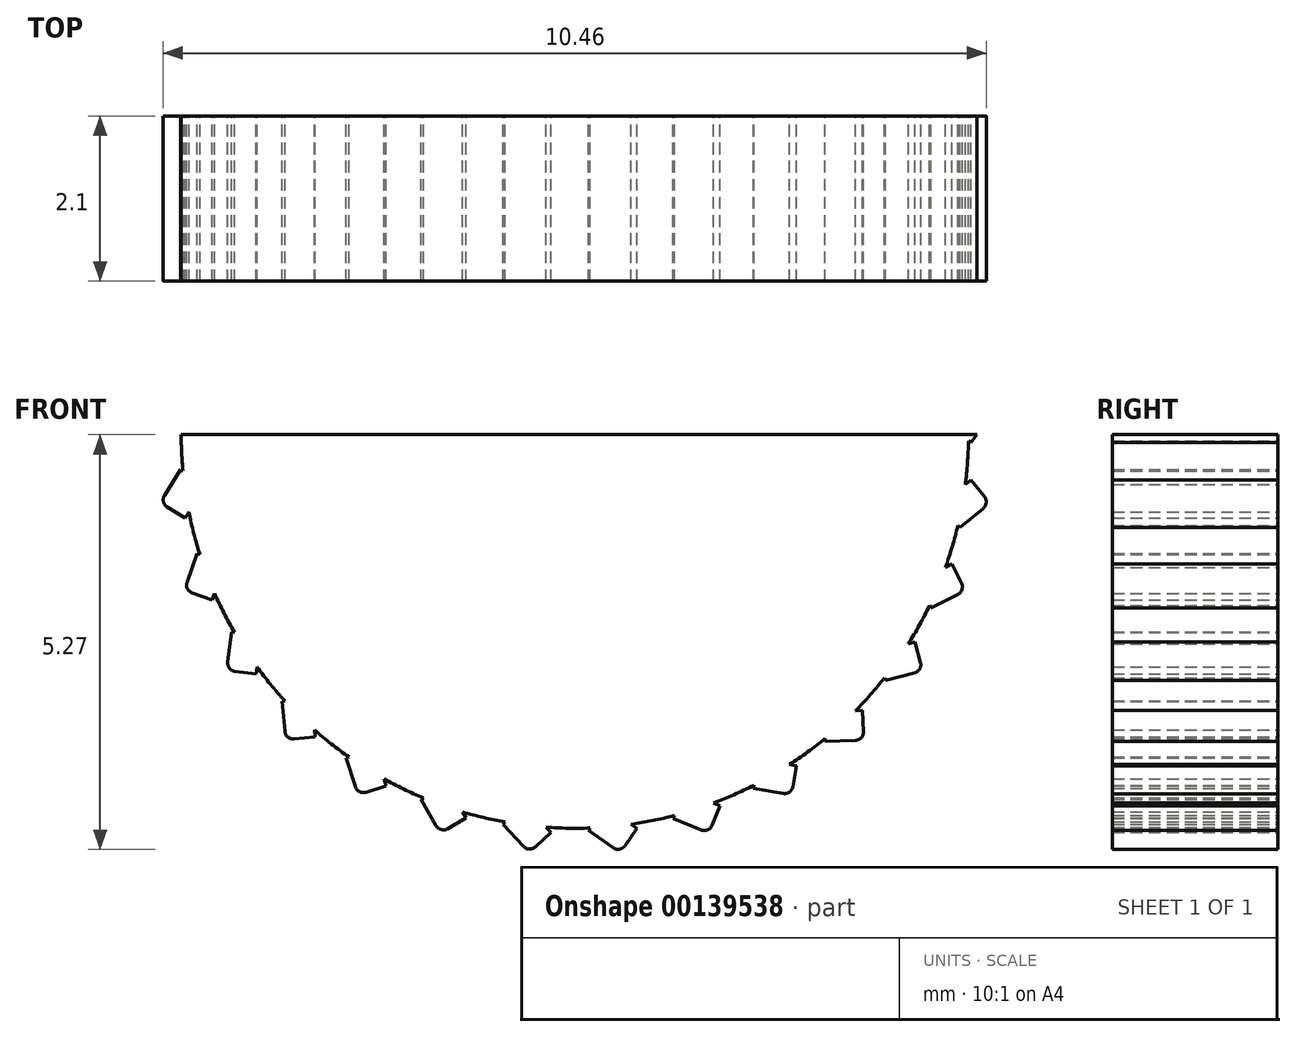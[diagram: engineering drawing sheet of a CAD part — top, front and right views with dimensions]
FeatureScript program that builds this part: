
annotation { "Feature Type Name" : "Feature", "Feature Type Description" : "" }
export const myFeature = defineFeature(function(context is Context, id is Id, definition is map)
    precondition{}
    {
        {
            var Q0;
            Q0=qCreatedBy(makeId("Front.planeOp"),FACE);
            var sketch = newSketch(context, id + "F0", { "sketchPlane" : qUnion([Q0])});
            skCircle(sketch, "E0", {"center": v(0, 0) * mm, "radius": 5 * mm});
            skPoint(sketch, "E1.0.29.0", {"position": v(-5.33, 0.3) * mm});
            skLineSegment(sketch, "E1.1.29.0", {"start": v(-4.72, 0.38) * mm, "end": v(-4.99, 0.64) * mm});
            skLineSegment(sketch, "E1.4.29.0", {"start": v(-5.26, 0.37) * mm, "end": v(-4.99, 0.64) * mm});
            skLineSegment(sketch, "E1.7.29.0", {"start": v(-5.06, 0.03) * mm, "end": v(-4.72, 0.38) * mm});
            skLineSegment(sketch, "E1.10.29.0", {"start": v(-5.06, 0.03) * mm, "end": v(-5.26, 0.22) * mm});
            skArc(sketch, "E1.13.29.0", {"start": v(-5.26, 0.37) * mm, "mid": v(-5.29, 0.3) * mm, "end": v(-5.26, 0.22) * mm});
            skPoint(sketch, "E2.1.0", {"position": v(-5.14, 1.43) * mm});
            skLineSegment(sketch, "E2.1.1", {"start": v(-4.94, 1.12) * mm, "end": v(-4.53, 1.39) * mm});
            skLineSegment(sketch, "E2.1.2", {"start": v(-4.94, 1.12) * mm, "end": v(-5.09, 1.34) * mm});
            skLineSegment(sketch, "E2.1.3", {"start": v(-4.53, 1.39) * mm, "end": v(-4.73, 1.7) * mm});
            skLineSegment(sketch, "E2.1.4", {"start": v(-5.06, 1.49) * mm, "end": v(-4.73, 1.7) * mm});
            skArc(sketch, "E2.1.5", {"start": v(-5.06, 1.49) * mm, "mid": v(-5.1, 1.42) * mm, "end": v(-5.09, 1.34) * mm});
            skPoint(sketch, "E2.2.0", {"position": v(-4.72, 2.5) * mm});
            skLineSegment(sketch, "E2.2.1", {"start": v(-4.58, 2.15) * mm, "end": v(-4.12, 2.33) * mm});
            skLineSegment(sketch, "E2.2.2", {"start": v(-4.58, 2.15) * mm, "end": v(-4.68, 2.4) * mm});
            skLineSegment(sketch, "E2.2.3", {"start": v(-4.12, 2.33) * mm, "end": v(-4.26, 2.68) * mm});
            skLineSegment(sketch, "E2.2.4", {"start": v(-4.62, 2.54) * mm, "end": v(-4.26, 2.68) * mm});
            skArc(sketch, "E2.2.5", {"start": v(-4.62, 2.54) * mm, "mid": v(-4.68, 2.49) * mm, "end": v(-4.68, 2.4) * mm});
            skPoint(sketch, "E2.3.0", {"position": v(-4.07, 3.46) * mm});
            skLineSegment(sketch, "E2.3.1", {"start": v(-4.01, 3.09) * mm, "end": v(-3.53, 3.16) * mm});
            skLineSegment(sketch, "E2.3.2", {"start": v(-4.01, 3.09) * mm, "end": v(-4.05, 3.35) * mm});
            skLineSegment(sketch, "E2.3.3", {"start": v(-3.53, 3.16) * mm, "end": v(-3.58, 3.53) * mm});
            skLineSegment(sketch, "E2.3.4", {"start": v(-3.96, 3.47) * mm, "end": v(-3.58, 3.53) * mm});
            skArc(sketch, "E2.3.5", {"start": v(-3.96, 3.47) * mm, "mid": v(-4.03, 3.43) * mm, "end": v(-4.05, 3.35) * mm});
            skPoint(sketch, "E2.4.0", {"position": v(-3.23, 4.25) * mm});
            skLineSegment(sketch, "E2.4.1", {"start": v(-3.25, 3.88) * mm, "end": v(-2.76, 3.84) * mm});
            skLineSegment(sketch, "E2.4.2", {"start": v(-3.25, 3.88) * mm, "end": v(-3.24, 4.15) * mm});
            skLineSegment(sketch, "E2.4.3", {"start": v(-2.76, 3.84) * mm, "end": v(-2.74, 4.22) * mm});
            skLineSegment(sketch, "E2.4.4", {"start": v(-3.12, 4.25) * mm, "end": v(-2.74, 4.22) * mm});
            skArc(sketch, "E2.4.5", {"start": v(-3.12, 4.25) * mm, "mid": v(-3.2, 4.22) * mm, "end": v(-3.24, 4.15) * mm});
            skPoint(sketch, "E2.5.0", {"position": v(-2.24, 4.85) * mm});
            skLineSegment(sketch, "E2.5.1", {"start": v(-2.34, 4.49) * mm, "end": v(-1.87, 4.35) * mm});
            skLineSegment(sketch, "E2.5.2", {"start": v(-2.34, 4.49) * mm, "end": v(-2.27, 4.75) * mm});
            skLineSegment(sketch, "E2.5.3", {"start": v(-1.87, 4.35) * mm, "end": v(-1.77, 4.7) * mm});
            skLineSegment(sketch, "E2.5.4", {"start": v(-2.14, 4.82) * mm, "end": v(-1.77, 4.7) * mm});
            skArc(sketch, "E2.5.5", {"start": v(-2.14, 4.82) * mm, "mid": v(-2.22, 4.8) * mm, "end": v(-2.27, 4.75) * mm});
            skPoint(sketch, "E2.6.0", {"position": v(-1.15, 5.22) * mm});
            skLineSegment(sketch, "E2.6.1", {"start": v(-1.33, 4.89) * mm, "end": v(-0.9, 4.65) * mm});
            skLineSegment(sketch, "E2.6.2", {"start": v(-1.33, 4.89) * mm, "end": v(-1.2, 5.12) * mm});
            skLineSegment(sketch, "E2.6.3", {"start": v(-0.9, 4.65) * mm, "end": v(-0.71, 4.98) * mm});
            skLineSegment(sketch, "E2.6.4", {"start": v(-1.05, 5.16) * mm, "end": v(-0.71, 4.98) * mm});
            skArc(sketch, "E2.6.5", {"start": v(-1.05, 5.16) * mm, "mid": v(-1.13, 5.17) * mm, "end": v(-1.2, 5.12) * mm});
            skPoint(sketch, "E2.7.0", {"position": v(0, 5.34) * mm});
            skLineSegment(sketch, "E2.7.1", {"start": v(-0.24, 5.06) * mm, "end": v(0.13, 4.73) * mm});
            skLineSegment(sketch, "E2.7.2", {"start": v(-0.24, 5.06) * mm, "end": v(-0.07, 5.26) * mm});
            skLineSegment(sketch, "E2.7.3", {"start": v(0.13, 4.73) * mm, "end": v(0.37, 5.02) * mm});
            skLineSegment(sketch, "E2.7.4", {"start": v(0.08, 5.27) * mm, "end": v(0.37, 5.02) * mm});
            skArc(sketch, "E2.7.5", {"start": v(0.08, 5.27) * mm, "mid": v(0, 5.3) * mm, "end": v(-0.07, 5.26) * mm});
            skPoint(sketch, "E2.8.0", {"position": v(1.15, 5.21) * mm});
            skLineSegment(sketch, "E2.8.1", {"start": v(0.85, 5) * mm, "end": v(1.14, 4.6) * mm});
            skLineSegment(sketch, "E2.8.2", {"start": v(0.85, 5) * mm, "end": v(1.07, 5.15) * mm});
            skLineSegment(sketch, "E2.8.3", {"start": v(1.14, 4.6) * mm, "end": v(1.44, 4.82) * mm});
            skLineSegment(sketch, "E2.8.4", {"start": v(1.21, 5.13) * mm, "end": v(1.44, 4.82) * mm});
            skArc(sketch, "E2.8.5", {"start": v(1.21, 5.13) * mm, "mid": v(1.14, 5.17) * mm, "end": v(1.07, 5.15) * mm});
            skPoint(sketch, "E2.9.0", {"position": v(2.24, 4.84) * mm});
            skLineSegment(sketch, "E2.9.1", {"start": v(1.9, 4.7) * mm, "end": v(2.1, 4.24) * mm});
            skLineSegment(sketch, "E2.9.2", {"start": v(1.9, 4.7) * mm, "end": v(2.15, 4.8) * mm});
            skLineSegment(sketch, "E2.9.3", {"start": v(2.1, 4.24) * mm, "end": v(2.45, 4.4) * mm});
            skLineSegment(sketch, "E2.9.4", {"start": v(2.29, 4.75) * mm, "end": v(2.45, 4.4) * mm});
            skArc(sketch, "E2.9.5", {"start": v(2.29, 4.75) * mm, "mid": v(2.23, 4.8) * mm, "end": v(2.15, 4.8) * mm});
            skPoint(sketch, "E2.10.0", {"position": v(3.23, 4.25) * mm});
            skLineSegment(sketch, "E2.10.1", {"start": v(2.87, 4.17) * mm, "end": v(2.96, 3.7) * mm});
            skLineSegment(sketch, "E2.10.2", {"start": v(2.87, 4.17) * mm, "end": v(3.13, 4.23) * mm});
            skLineSegment(sketch, "E2.10.3", {"start": v(2.96, 3.7) * mm, "end": v(3.33, 3.77) * mm});
            skLineSegment(sketch, "E2.10.4", {"start": v(3.25, 4.15) * mm, "end": v(3.33, 3.77) * mm});
            skArc(sketch, "E2.10.5", {"start": v(3.25, 4.15) * mm, "mid": v(3.2, 4.21) * mm, "end": v(3.13, 4.23) * mm});
            skPoint(sketch, "E2.11.0", {"position": v(4.07, 3.45) * mm});
            skLineSegment(sketch, "E2.11.1", {"start": v(3.7, 3.46) * mm, "end": v(3.69, 2.97) * mm});
            skLineSegment(sketch, "E2.11.2", {"start": v(3.7, 3.46) * mm, "end": v(3.97, 3.46) * mm});
            skLineSegment(sketch, "E2.11.3", {"start": v(3.69, 2.97) * mm, "end": v(4.07, 2.96) * mm});
            skLineSegment(sketch, "E2.11.4", {"start": v(4.07, 3.35) * mm, "end": v(4.07, 2.96) * mm});
            skArc(sketch, "E2.11.5", {"start": v(4.07, 3.35) * mm, "mid": v(4.04, 3.42) * mm, "end": v(3.97, 3.46) * mm});
            skPoint(sketch, "E2.12.0", {"position": v(4.72, 2.5) * mm});
            skLineSegment(sketch, "E2.12.1", {"start": v(4.35, 2.58) * mm, "end": v(4.24, 2.1) * mm});
            skLineSegment(sketch, "E2.12.2", {"start": v(4.35, 2.58) * mm, "end": v(4.62, 2.52) * mm});
            skLineSegment(sketch, "E2.12.3", {"start": v(4.24, 2.1) * mm, "end": v(4.6, 2.02) * mm});
            skLineSegment(sketch, "E2.12.4", {"start": v(4.7, 2.4) * mm, "end": v(4.6, 2.02) * mm});
            skArc(sketch, "E2.12.5", {"start": v(4.7, 2.4) * mm, "mid": v(4.68, 2.48) * mm, "end": v(4.62, 2.52) * mm});
            skPoint(sketch, "E2.13.0", {"position": v(5.15, 1.43) * mm});
            skLineSegment(sketch, "E2.13.1", {"start": v(4.8, 1.59) * mm, "end": v(4.6, 1.14) * mm});
            skLineSegment(sketch, "E2.13.2", {"start": v(4.8, 1.59) * mm, "end": v(5.05, 1.47) * mm});
            skLineSegment(sketch, "E2.13.3", {"start": v(4.6, 1.14) * mm, "end": v(4.93, 0.98) * mm});
            skLineSegment(sketch, "E2.13.4", {"start": v(5.1, 1.33) * mm, "end": v(4.93, 0.98) * mm});
            skArc(sketch, "E2.13.5", {"start": v(5.1, 1.33) * mm, "mid": v(5.1, 1.41) * mm, "end": v(5.05, 1.47) * mm});
            skPoint(sketch, "E2.14.0", {"position": v(5.33, 0.29) * mm});
            skLineSegment(sketch, "E2.14.1", {"start": v(5.04, 0.52) * mm, "end": v(4.73, 0.13) * mm});
            skLineSegment(sketch, "E2.14.2", {"start": v(5.04, 0.52) * mm, "end": v(5.25, 0.35) * mm});
            skLineSegment(sketch, "E2.14.3", {"start": v(4.73, 0.13) * mm, "end": v(5.03, -0.1) * mm});
            skLineSegment(sketch, "E2.14.4", {"start": v(5.27, 0.2) * mm, "end": v(5.03, -0.1) * mm});
            skArc(sketch, "E2.14.5", {"start": v(5.27, 0.2) * mm, "mid": v(5.29, 0.28) * mm, "end": v(5.25, 0.35) * mm});
            skPoint(sketch, "E2.15.0", {"position": v(5.27, -0.87) * mm});
            skLineSegment(sketch, "E2.15.1", {"start": v(5.03, -0.58) * mm, "end": v(4.65, -0.9) * mm});
            skLineSegment(sketch, "E2.15.2", {"start": v(5.03, -0.58) * mm, "end": v(5.2, -0.78) * mm});
            skLineSegment(sketch, "E2.15.3", {"start": v(4.65, -0.9) * mm, "end": v(4.9, -1.18) * mm});
            skLineSegment(sketch, "E2.15.4", {"start": v(5.19, -0.93) * mm, "end": v(4.9, -1.18) * mm});
            skArc(sketch, "E2.15.5", {"start": v(5.19, -0.93) * mm, "mid": v(5.23, -0.86) * mm, "end": v(5.2, -0.78) * mm});
            skPoint(sketch, "E2.16.0", {"position": v(4.96, -1.98) * mm});
            skLineSegment(sketch, "E2.16.1", {"start": v(4.79, -1.64) * mm, "end": v(4.35, -1.87) * mm});
            skLineSegment(sketch, "E2.16.2", {"start": v(4.79, -1.64) * mm, "end": v(4.91, -1.88) * mm});
            skLineSegment(sketch, "E2.16.3", {"start": v(4.35, -1.87) * mm, "end": v(4.52, -2.2) * mm});
            skLineSegment(sketch, "E2.16.4", {"start": v(4.87, -2.03) * mm, "end": v(4.52, -2.2) * mm});
            skArc(sketch, "E2.16.5", {"start": v(4.87, -2.03) * mm, "mid": v(4.92, -1.97) * mm, "end": v(4.91, -1.88) * mm});
            skPoint(sketch, "E2.17.0", {"position": v(4.42, -3) * mm});
            skLineSegment(sketch, "E2.17.1", {"start": v(4.32, -2.64) * mm, "end": v(3.85, -2.76) * mm});
            skLineSegment(sketch, "E2.17.2", {"start": v(4.32, -2.64) * mm, "end": v(4.4, -2.9) * mm});
            skLineSegment(sketch, "E2.17.3", {"start": v(3.85, -2.76) * mm, "end": v(3.94, -3.12) * mm});
            skLineSegment(sketch, "E2.17.4", {"start": v(4.32, -3.03) * mm, "end": v(3.94, -3.12) * mm});
            skArc(sketch, "E2.17.5", {"start": v(4.32, -3.03) * mm, "mid": v(4.38, -2.98) * mm, "end": v(4.4, -2.9) * mm});
            skPoint(sketch, "E2.18.0", {"position": v(3.67, -3.88) * mm});
            skLineSegment(sketch, "E2.18.1", {"start": v(3.65, -3.5) * mm, "end": v(3.16, -3.52) * mm});
            skLineSegment(sketch, "E2.18.2", {"start": v(3.65, -3.5) * mm, "end": v(3.67, -3.77) * mm});
            skLineSegment(sketch, "E2.18.3", {"start": v(3.16, -3.52) * mm, "end": v(3.18, -3.9) * mm});
            skLineSegment(sketch, "E2.18.4", {"start": v(3.56, -3.88) * mm, "end": v(3.18, -3.9) * mm});
            skArc(sketch, "E2.18.5", {"start": v(3.56, -3.88) * mm, "mid": v(3.64, -3.85) * mm, "end": v(3.67, -3.77) * mm});
            skPoint(sketch, "E2.19.0", {"position": v(2.75, -4.58) * mm});
            skLineSegment(sketch, "E2.19.1", {"start": v(2.82, -4.2) * mm, "end": v(2.33, -4.12) * mm});
            skLineSegment(sketch, "E2.19.2", {"start": v(2.82, -4.2) * mm, "end": v(2.77, -4.47) * mm});
            skLineSegment(sketch, "E2.19.3", {"start": v(2.33, -4.12) * mm, "end": v(2.27, -4.5) * mm});
            skLineSegment(sketch, "E2.19.4", {"start": v(2.65, -4.56) * mm, "end": v(2.27, -4.5) * mm});
            skArc(sketch, "E2.19.5", {"start": v(2.65, -4.56) * mm, "mid": v(2.73, -4.54) * mm, "end": v(2.77, -4.47) * mm});
            skLineSegment(sketch, "E2.anchor1", {"start": v(0, 0) * mm, "end": v(-5.33, 0.3) * mm, "construction": true});
            skLineSegment(sketch, "E2.anchor2", {"start": v(0, 0) * mm, "end": v(-5.33, 0.3) * mm, "construction": true});
            skPoint(sketch, "E3.0.20.0", {"position": v(1.7, -5.06) * mm});
            skLineSegment(sketch, "E3.1.20.0", {"start": v(1.85, -4.71) * mm, "end": v(1.4, -4.53) * mm});
            skLineSegment(sketch, "E3.4.20.0", {"start": v(1.85, -4.71) * mm, "end": v(1.74, -4.96) * mm});
            skLineSegment(sketch, "E3.7.20.0", {"start": v(1.4, -4.53) * mm, "end": v(1.25, -4.87) * mm});
            skLineSegment(sketch, "E3.10.20.0", {"start": v(1.6, -5.02) * mm, "end": v(1.25, -4.87) * mm});
            skArc(sketch, "E3.13.20.0", {"start": v(1.6, -5.02) * mm, "mid": v(1.69, -5.02) * mm, "end": v(1.74, -4.96) * mm});
            skPoint(sketch, "E3.0.21.0", {"position": v(0.57, -5.3) * mm});
            skLineSegment(sketch, "E3.1.21.0", {"start": v(0.79, -5) * mm, "end": v(0.39, -4.72) * mm});
            skLineSegment(sketch, "E3.4.21.0", {"start": v(0.79, -5) * mm, "end": v(0.64, -5.22) * mm});
            skLineSegment(sketch, "E3.7.21.0", {"start": v(0.39, -4.72) * mm, "end": v(0.17, -5.03) * mm});
            skLineSegment(sketch, "E3.10.21.0", {"start": v(0.49, -5.25) * mm, "end": v(0.17, -5.03) * mm});
            skArc(sketch, "E3.13.21.0", {"start": v(0.49, -5.25) * mm, "mid": v(0.57, -5.27) * mm, "end": v(0.64, -5.22) * mm});
            skPoint(sketch, "E3.0.22.0", {"position": v(-0.58, -5.3) * mm});
            skLineSegment(sketch, "E3.1.22.0", {"start": v(-0.3, -5.05) * mm, "end": v(-0.64, -4.7) * mm});
            skLineSegment(sketch, "E3.4.22.0", {"start": v(-0.3, -5.05) * mm, "end": v(-0.5, -5.24) * mm});
            skLineSegment(sketch, "E3.7.22.0", {"start": v(-0.64, -4.7) * mm, "end": v(-0.91, -4.95) * mm});
            skLineSegment(sketch, "E3.10.22.0", {"start": v(-0.65, -5.23) * mm, "end": v(-0.91, -4.95) * mm});
            skArc(sketch, "E3.13.22.0", {"start": v(-0.65, -5.23) * mm, "mid": v(-0.58, -5.26) * mm, "end": v(-0.5, -5.24) * mm});
            skPoint(sketch, "E3.0.23.0", {"position": v(-1.7, -5.06) * mm});
            skLineSegment(sketch, "E3.1.23.0", {"start": v(-1.38, -4.87) * mm, "end": v(-1.63, -4.45) * mm});
            skLineSegment(sketch, "E3.4.23.0", {"start": v(-1.38, -4.87) * mm, "end": v(-1.62, -5) * mm});
            skLineSegment(sketch, "E3.7.23.0", {"start": v(-1.63, -4.45) * mm, "end": v(-1.96, -4.64) * mm});
            skLineSegment(sketch, "E3.10.23.0", {"start": v(-1.76, -4.97) * mm, "end": v(-1.96, -4.64) * mm});
            skArc(sketch, "E3.13.23.0", {"start": v(-1.76, -4.97) * mm, "mid": v(-1.7, -5.02) * mm, "end": v(-1.62, -5) * mm});
            skPoint(sketch, "E3.0.24.0", {"position": v(-2.75, -4.57) * mm});
            skLineSegment(sketch, "E3.1.24.0", {"start": v(-2.4, -4.46) * mm, "end": v(-2.55, -4) * mm});
            skLineSegment(sketch, "E3.4.24.0", {"start": v(-2.4, -4.46) * mm, "end": v(-2.65, -4.54) * mm});
            skLineSegment(sketch, "E3.7.24.0", {"start": v(-2.55, -4) * mm, "end": v(-2.9, -4.1) * mm});
            skLineSegment(sketch, "E3.10.24.0", {"start": v(-2.79, -4.47) * mm, "end": v(-2.9, -4.1) * mm});
            skArc(sketch, "E3.13.24.0", {"start": v(-2.79, -4.47) * mm, "mid": v(-2.74, -4.53) * mm, "end": v(-2.65, -4.54) * mm});
            skPoint(sketch, "E3.0.25.0", {"position": v(-3.67, -3.87) * mm});
            skLineSegment(sketch, "E3.1.25.0", {"start": v(-3.3, -3.84) * mm, "end": v(-3.35, -3.35) * mm});
            skLineSegment(sketch, "E3.4.25.0", {"start": v(-3.3, -3.84) * mm, "end": v(-3.57, -3.86) * mm});
            skLineSegment(sketch, "E3.7.25.0", {"start": v(-3.35, -3.35) * mm, "end": v(-3.72, -3.39) * mm});
            skLineSegment(sketch, "E3.10.25.0", {"start": v(-3.68, -3.77) * mm, "end": v(-3.72, -3.39) * mm});
            skArc(sketch, "E3.13.25.0", {"start": v(-3.68, -3.77) * mm, "mid": v(-3.65, -3.84) * mm, "end": v(-3.57, -3.86) * mm});
            skPoint(sketch, "E3.0.26.0", {"position": v(-4.42, -3) * mm});
            skLineSegment(sketch, "E3.1.26.0", {"start": v(-4.05, -3.04) * mm, "end": v(-3.99, -2.55) * mm});
            skLineSegment(sketch, "E3.4.26.0", {"start": v(-4.05, -3.04) * mm, "end": v(-4.32, -3) * mm});
            skLineSegment(sketch, "E3.7.26.0", {"start": v(-3.99, -2.55) * mm, "end": v(-4.36, -2.5) * mm});
            skLineSegment(sketch, "E3.10.26.0", {"start": v(-4.4, -2.89) * mm, "end": v(-4.36, -2.5) * mm});
            skArc(sketch, "E3.13.26.0", {"start": v(-4.4, -2.89) * mm, "mid": v(-4.39, -2.97) * mm, "end": v(-4.32, -3) * mm});
            skPoint(sketch, "E3.0.27.0", {"position": v(-4.96, -1.97) * mm});
            skLineSegment(sketch, "E3.1.27.0", {"start": v(-4.6, -2.1) * mm, "end": v(-4.44, -1.63) * mm});
            skLineSegment(sketch, "E3.4.27.0", {"start": v(-4.6, -2.1) * mm, "end": v(-4.86, -2) * mm});
            skLineSegment(sketch, "E3.7.27.0", {"start": v(-4.44, -1.63) * mm, "end": v(-4.8, -1.51) * mm});
            skLineSegment(sketch, "E3.10.27.0", {"start": v(-4.93, -1.87) * mm, "end": v(-4.8, -1.51) * mm});
            skArc(sketch, "E3.13.27.0", {"start": v(-4.93, -1.87) * mm, "mid": v(-4.92, -1.96) * mm, "end": v(-4.86, -2) * mm});
            skPoint(sketch, "E3.0.28.0", {"position": v(-5.27, -0.86) * mm});
            skLineSegment(sketch, "E3.1.28.0", {"start": v(-4.95, -1.06) * mm, "end": v(-4.7, -0.64) * mm});
            skLineSegment(sketch, "E3.4.28.0", {"start": v(-4.95, -1.06) * mm, "end": v(-5.18, -0.92) * mm});
            skLineSegment(sketch, "E3.7.28.0", {"start": v(-4.7, -0.64) * mm, "end": v(-5.01, -0.44) * mm});
            skLineSegment(sketch, "E3.10.28.0", {"start": v(-5.21, -0.77) * mm, "end": v(-5.01, -0.44) * mm});
            skArc(sketch, "E3.13.28.0", {"start": v(-5.21, -0.77) * mm, "mid": v(-5.23, -0.85) * mm, "end": v(-5.18, -0.92) * mm});
            skSolve(sketch);
        }
        {
            var Q0;
            Q0 = qSketchRegion(id + "F0", true);
            extrude(context, id + "F1", {"entities" : qUnion([Q0]), "depth" : 2.1 * mm});
        }
        {
            var Q0;
            Q0=makeQuery(id+"F1.opExtrude","CAP_FACE",FACE,{"disambiguationData":[OSD([sQuery(id+"F0.wireOp",EDGE,"E0"),sQuery(id+"F0.wireOp",EDGE,"ySS5cQUZ-Fo5e-DXVH-MhZB-vUoRHThh9X3S.top"),sQuery(id+"F0.wireOp",EDGE,"ySS5cQUZ-Fo5e-DXVH-MhZB-vUoRHThh9X3S.left"),sQuery(id+"F0.wireOp",EDGE,"ySS5cQUZ-Fo5e-DXVH-MhZB-vUoRHThh9X3S.right"),sQuery(id+"F0.wireOp",EDGE,"424ddff2-87a4-4609-a369-d8ad4bc9802c.1.0"),sQuery(id+"F0.wireOp",EDGE,"424ddff2-87a4-4609-a369-d8ad4bc9802c.1.1"),sQuery(id+"F0.wireOp",EDGE,"424ddff2-87a4-4609-a369-d8ad4bc9802c.1.3"),sQuery(id+"F0.wireOp",EDGE,"424ddff2-87a4-4609-a369-d8ad4bc9802c.2.0"),sQuery(id+"F0.wireOp",EDGE,"424ddff2-87a4-4609-a369-d8ad4bc9802c.2.1"),sQuery(id+"F0.wireOp",EDGE,"424ddff2-87a4-4609-a369-d8ad4bc9802c.2.3"),sQuery(id+"F0.wireOp",EDGE,"424ddff2-87a4-4609-a369-d8ad4bc9802c.3.0"),sQuery(id+"F0.wireOp",EDGE,"424ddff2-87a4-4609-a369-d8ad4bc9802c.3.1"),sQuery(id+"F0.wireOp",EDGE,"424ddff2-87a4-4609-a369-d8ad4bc9802c.3.3"),sQuery(id+"F0.wireOp",EDGE,"424ddff2-87a4-4609-a369-d8ad4bc9802c.4.0"),sQuery(id+"F0.wireOp",EDGE,"424ddff2-87a4-4609-a369-d8ad4bc9802c.4.1"),sQuery(id+"F0.wireOp",EDGE,"424ddff2-87a4-4609-a369-d8ad4bc9802c.4.3"),sQuery(id+"F0.wireOp",EDGE,"424ddff2-87a4-4609-a369-d8ad4bc9802c.5.0"),sQuery(id+"F0.wireOp",EDGE,"424ddff2-87a4-4609-a369-d8ad4bc9802c.5.1"),sQuery(id+"F0.wireOp",EDGE,"424ddff2-87a4-4609-a369-d8ad4bc9802c.5.3"),sQuery(id+"F0.wireOp",EDGE,"424ddff2-87a4-4609-a369-d8ad4bc9802c.6.0"),sQuery(id+"F0.wireOp",EDGE,"424ddff2-87a4-4609-a369-d8ad4bc9802c.6.1"),sQuery(id+"F0.wireOp",EDGE,"424ddff2-87a4-4609-a369-d8ad4bc9802c.6.3"),sQuery(id+"F0.wireOp",EDGE,"424ddff2-87a4-4609-a369-d8ad4bc9802c.7.0"),sQuery(id+"F0.wireOp",EDGE,"424ddff2-87a4-4609-a369-d8ad4bc9802c.7.1"),sQuery(id+"F0.wireOp",EDGE,"424ddff2-87a4-4609-a369-d8ad4bc9802c.7.3"),sQuery(id+"F0.wireOp",EDGE,"424ddff2-87a4-4609-a369-d8ad4bc9802c.8.0"),sQuery(id+"F0.wireOp",EDGE,"424ddff2-87a4-4609-a369-d8ad4bc9802c.8.1"),sQuery(id+"F0.wireOp",EDGE,"424ddff2-87a4-4609-a369-d8ad4bc9802c.8.3"),sQuery(id+"F0.wireOp",EDGE,"424ddff2-87a4-4609-a369-d8ad4bc9802c.9.0"),sQuery(id+"F0.wireOp",EDGE,"424ddff2-87a4-4609-a369-d8ad4bc9802c.9.1"),sQuery(id+"F0.wireOp",EDGE,"424ddff2-87a4-4609-a369-d8ad4bc9802c.9.3"),sQuery(id+"F0.wireOp",EDGE,"424ddff2-87a4-4609-a369-d8ad4bc9802c.10.0"),sQuery(id+"F0.wireOp",EDGE,"424ddff2-87a4-4609-a369-d8ad4bc9802c.10.1"),sQuery(id+"F0.wireOp",EDGE,"424ddff2-87a4-4609-a369-d8ad4bc9802c.10.3"),sQuery(id+"F0.wireOp",EDGE,"424ddff2-87a4-4609-a369-d8ad4bc9802c.11.0"),sQuery(id+"F0.wireOp",EDGE,"424ddff2-87a4-4609-a369-d8ad4bc9802c.11.1"),sQuery(id+"F0.wireOp",EDGE,"424ddff2-87a4-4609-a369-d8ad4bc9802c.11.3"),sQuery(id+"F0.wireOp",EDGE,"424ddff2-87a4-4609-a369-d8ad4bc9802c.12.0"),sQuery(id+"F0.wireOp",EDGE,"424ddff2-87a4-4609-a369-d8ad4bc9802c.12.1"),sQuery(id+"F0.wireOp",EDGE,"424ddff2-87a4-4609-a369-d8ad4bc9802c.12.3"),sQuery(id+"F0.wireOp",EDGE,"424ddff2-87a4-4609-a369-d8ad4bc9802c.13.0"),sQuery(id+"F0.wireOp",EDGE,"424ddff2-87a4-4609-a369-d8ad4bc9802c.13.1"),sQuery(id+"F0.wireOp",EDGE,"424ddff2-87a4-4609-a369-d8ad4bc9802c.13.3"),sQuery(id+"F0.wireOp",EDGE,"424ddff2-87a4-4609-a369-d8ad4bc9802c.14.0"),sQuery(id+"F0.wireOp",EDGE,"424ddff2-87a4-4609-a369-d8ad4bc9802c.14.1"),sQuery(id+"F0.wireOp",EDGE,"424ddff2-87a4-4609-a369-d8ad4bc9802c.14.3")])],"isStart":false});
            var sketch = newSketch(context, id + "F2", { "sketchPlane" : qUnion([Q0])});
            skPoint(sketch, "E4.startSnap0", {"position": v(4.95, 0.72) * mm});
            skPoint(sketch, "E5.orphan", {"position": v(3.48, 0.72) * mm});
            skLineSegment(sketch, "E6", {"start": v(18.2, 0) * mm, "end": v(-18.2, 0) * mm});
            skArc(sketch, "E7.MirrorCS", {"start": v(-18.2, 0) * mm, "mid": v(0, 18.2) * mm, "end": v(18.2, 0) * mm});
            skSolve(sketch);
        }
        {
            var Q0;
            Q0 = qSketchRegion(id + "F2", true);
            extrude(context, id + "F3", {"entities" : qUnion([Q0]), "operationType" : NewBodyOperationType.REMOVE, "endBound" : BoundingType.THROUGH_ALL, "oppositeDirection" : true, "depth" : 25 * mm});
        }
    });
